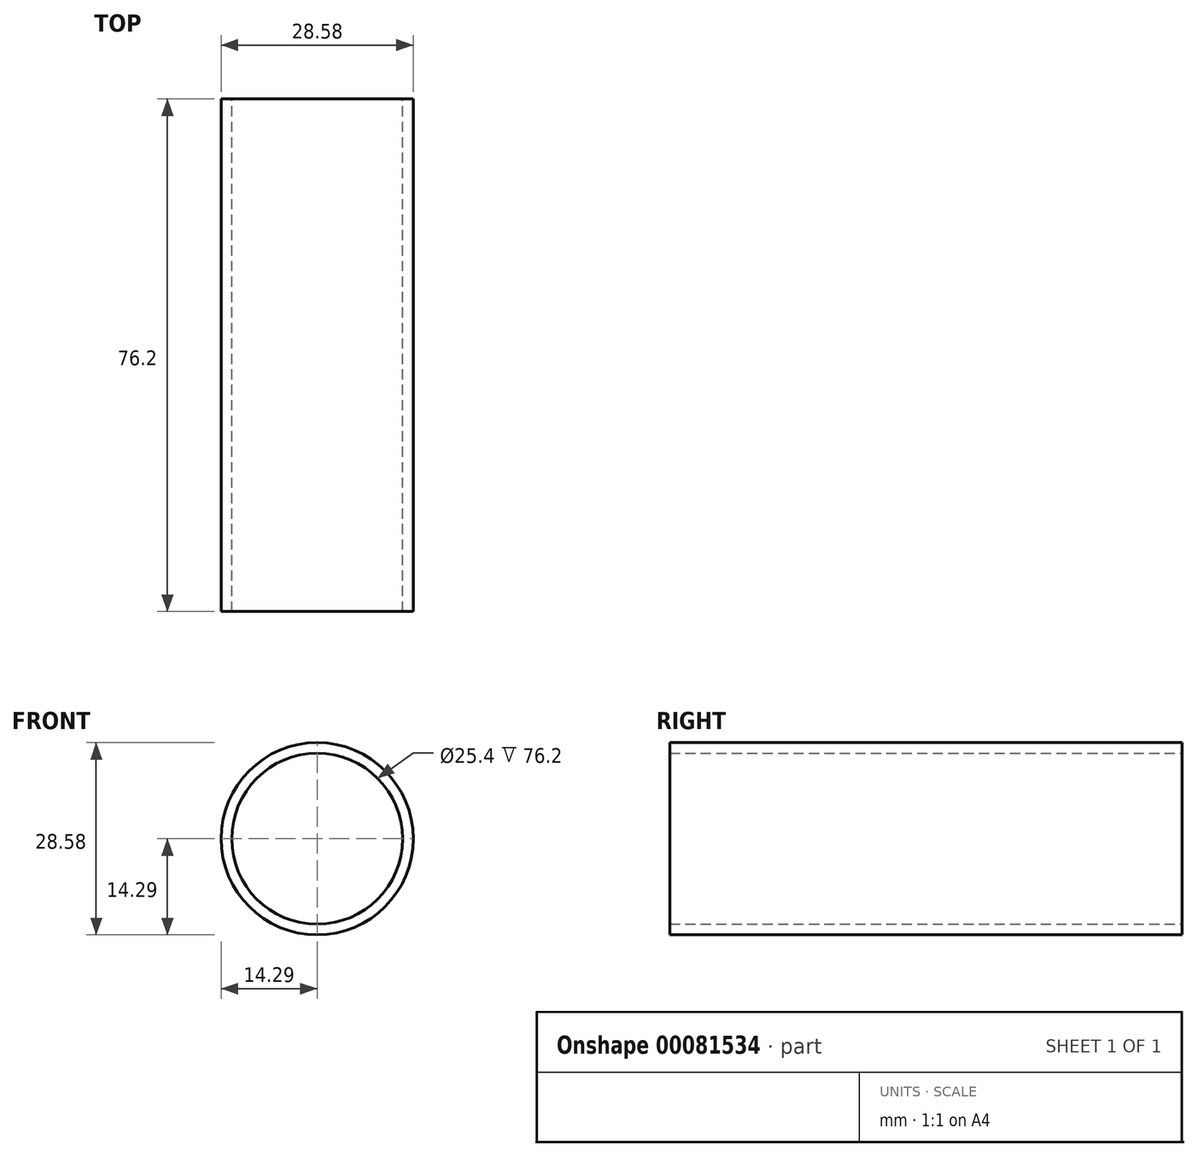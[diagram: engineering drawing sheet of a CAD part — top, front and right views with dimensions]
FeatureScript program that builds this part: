
annotation { "Feature Type Name" : "Feature", "Feature Type Description" : "" }
export const myFeature = defineFeature(function(context is Context, id is Id, definition is map)
    precondition{}
    {
        {
            var Q0;
            Q0=qCreatedBy(makeId("Front.planeOp"),FACE);
            var sketch = newSketch(context, id + "F0", { "sketchPlane" : qUnion([Q0])});
            skCircle(sketch, "E0", {"center": v(0, 0) * mm, "radius": 12.7 * mm});
            skCircle(sketch, "E1", {"center": v(0, 0) * mm, "radius": 14.29 * mm});
            skSolve(sketch);
        }
        {
            var Q0;
            Q0=makeQuery(id+"F0.imprint","IMPRINT",FACE,{"disambiguationData":[TD([[makeQuery(id+"F0.imprint","IMPRINT",EDGE,{"derivedFrom":sQuery(id+"F0.wireOp",EDGE,"E0")}),-1.0]])]});
            extrude(context, id + "F1", {"entities" : qUnion([Q0]), "depth" : 76.2 * mm});
        }
    });
